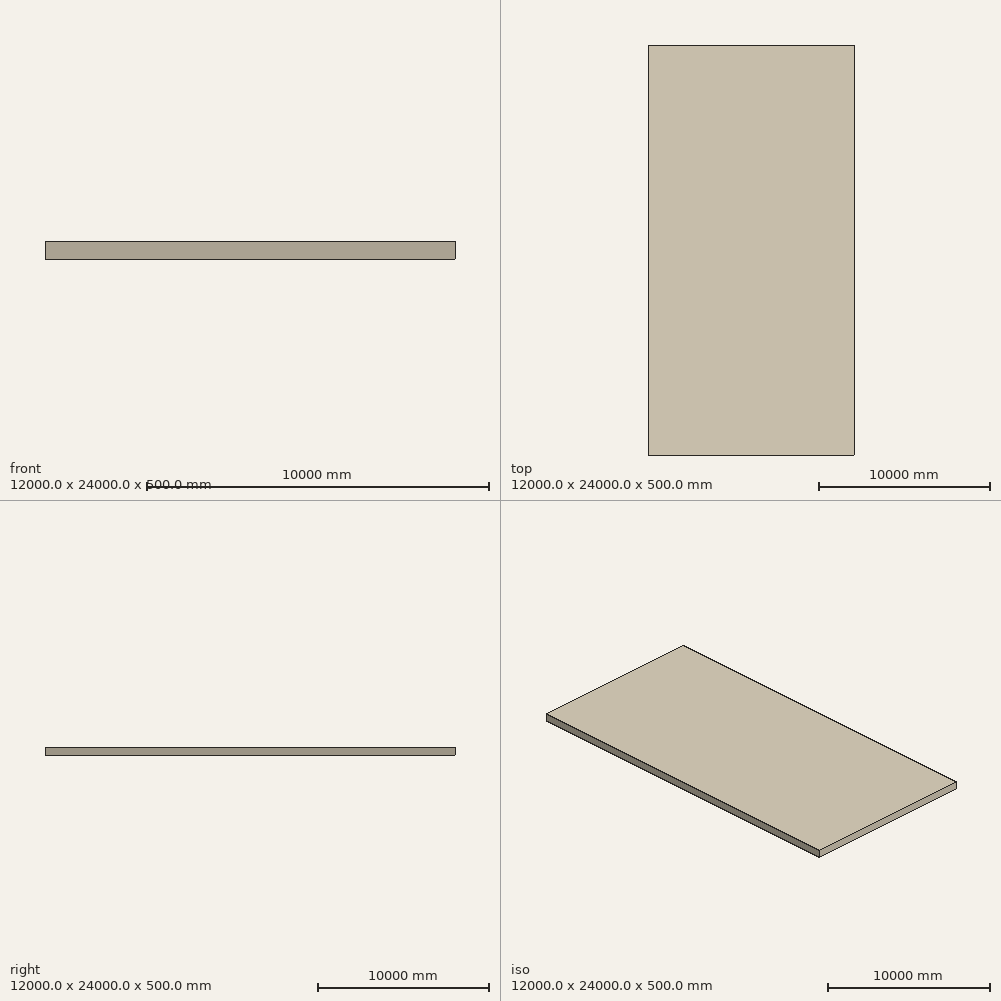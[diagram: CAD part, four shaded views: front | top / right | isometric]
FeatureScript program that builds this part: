
annotation { "Feature Type Name" : "Feature", "Feature Type Description" : "" }
export const myFeature = defineFeature(function(context is Context, id is Id, definition is map)
    precondition{}
    {
        {
            var Q0;
            Q0=qCreatedBy(makeId("Front.planeOp"),FACE);
            var sketch = newSketch(context, id + "F0", { "sketchPlane" : qUnion([Q0])});
            skLineSegment(sketch, "E0.bottom", {"start": v(-12000, 500) * mm, "end": v(0, 500) * mm});
            skLineSegment(sketch, "E0.top", {"start": v(-12000, 0) * mm, "end": v(0, 0) * mm});
            skLineSegment(sketch, "E0.left", {"start": v(-12000, 500) * mm, "end": v(-12000, 0) * mm});
            skLineSegment(sketch, "E0.right", {"start": v(0, 500) * mm, "end": v(0, 0) * mm});
            skSolve(sketch);
        }
        {
            var Q0;
            Q0=makeQuery(id+"F0.imprint","IMPRINT",FACE,{"disambiguationData":[TD([[makeQuery(id+"F0.imprint","IMPRINT",EDGE,{"derivedFrom":sQuery(id+"F0.wireOp",EDGE,"E0.bottom")}),-1.0]])]});
            extrude(context, id + "F1", {"entities" : qUnion([Q0]), "depth" : 24000 * mm});
        }
    });
